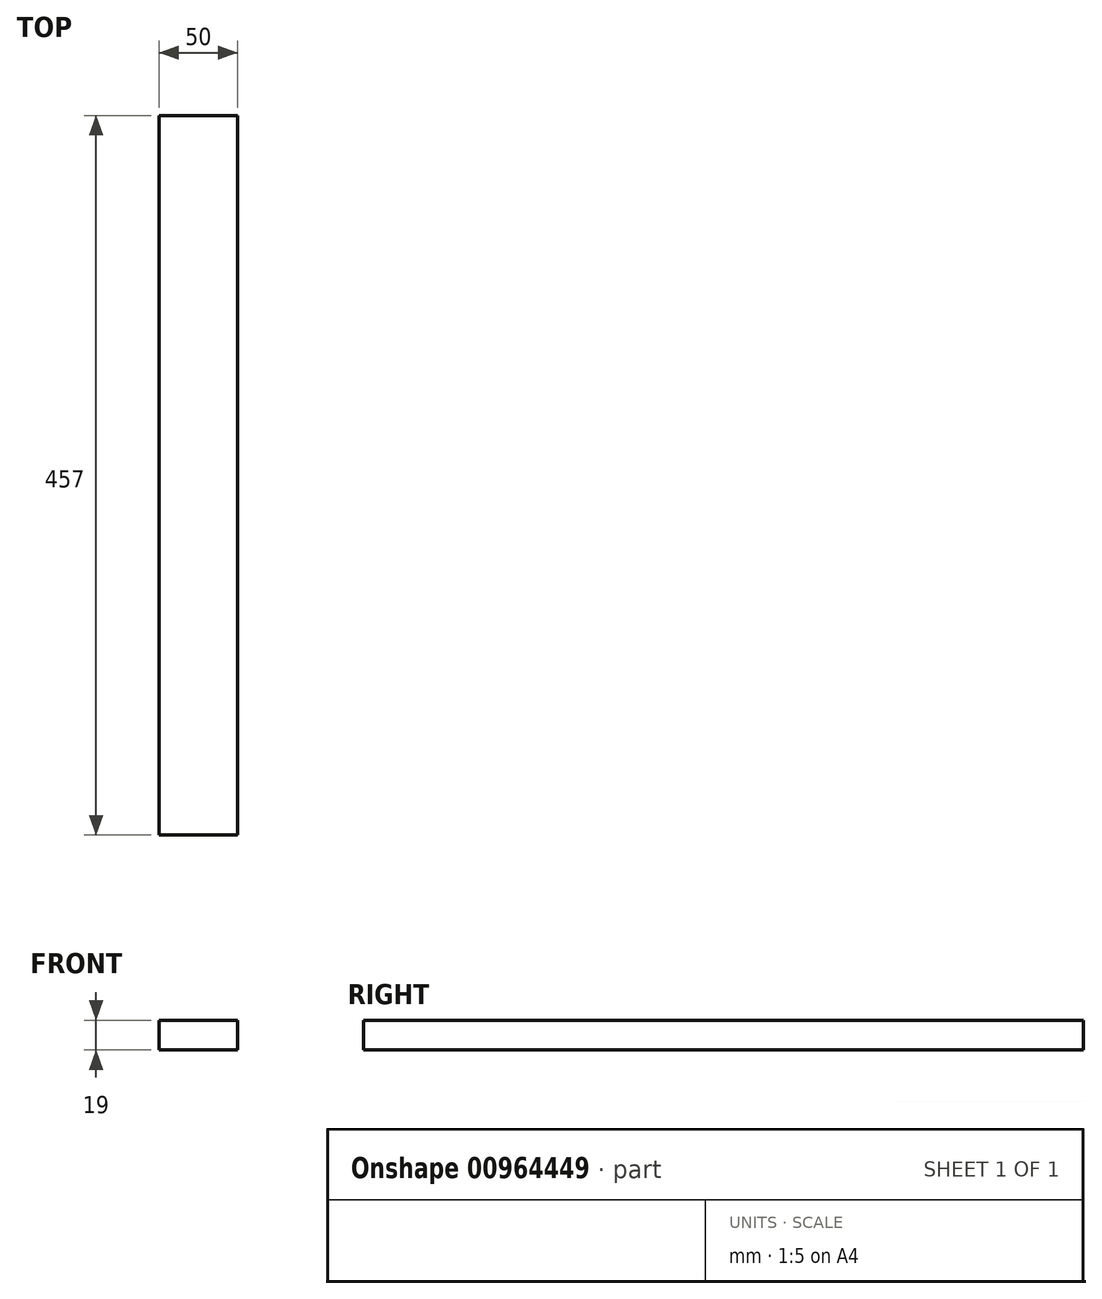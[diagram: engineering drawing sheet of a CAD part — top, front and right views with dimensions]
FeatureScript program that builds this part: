
annotation { "Feature Type Name" : "Feature", "Feature Type Description" : "" }
export const myFeature = defineFeature(function(context is Context, id is Id, definition is map)
    precondition{}
    {
        {
            var Q0;
            Q0=qCreatedBy(makeId("Front.planeOp"),FACE);
            var sketch = newSketch(context, id + "F0", { "sketchPlane" : qUnion([Q0])});
            skLineSegment(sketch, "E0.bottom", {"start": v(0, 0) * mm, "end": v(50, 0) * mm});
            skLineSegment(sketch, "E0.top", {"start": v(0, 19) * mm, "end": v(50, 19) * mm});
            skLineSegment(sketch, "E0.left", {"start": v(0, 0) * mm, "end": v(0, 19) * mm});
            skLineSegment(sketch, "E0.right", {"start": v(50, 0) * mm, "end": v(50, 19) * mm});
            skSolve(sketch);
        }
        {
            var Q0;
            Q0 = qSketchRegion(id + "F0", true);
            extrude(context, id + "F1", {"entities" : qUnion([Q0]), "oppositeDirection" : true, "depth" : 457 * mm, "offsetDistance" : 25 * mm});
        }
    });
